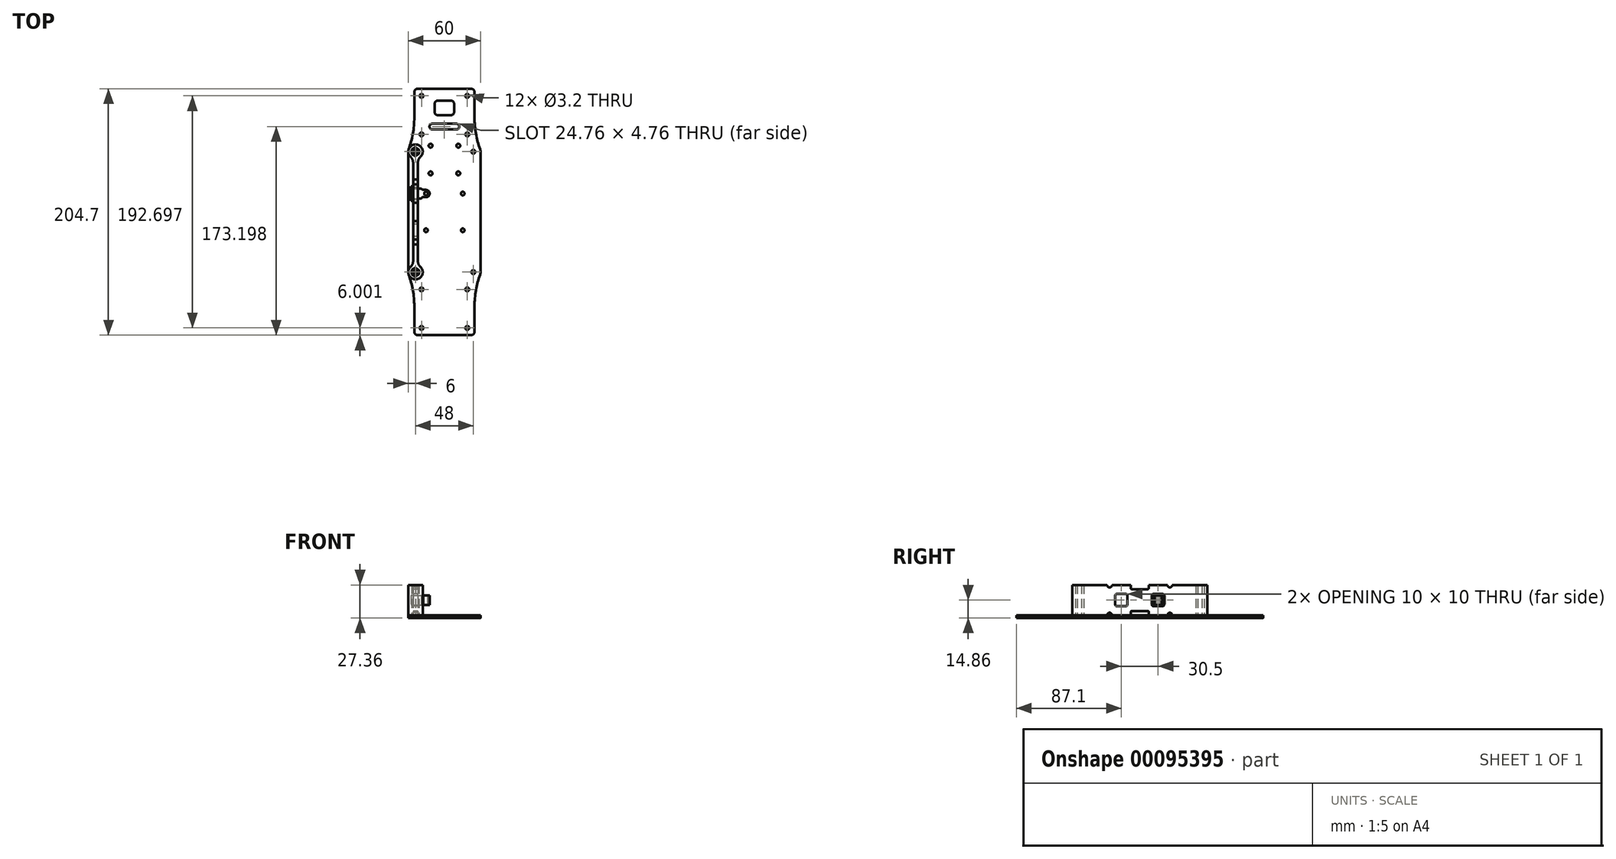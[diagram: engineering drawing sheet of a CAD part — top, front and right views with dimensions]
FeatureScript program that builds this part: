
annotation { "Feature Type Name" : "Feature", "Feature Type Description" : "" }
export const myFeature = defineFeature(function(context is Context, id is Id, definition is map)
    precondition{}
    {
        {
            var Q0;
            Q0=qCreatedBy(makeId("Top.planeOp"),FACE);
            var sketch = newSketch(context, id + "F0", { "sketchPlane" : qUnion([Q0])});
            skLineSegment(sketch, "E0", {"start": v(0, 102.35) * mm, "end": v(-22, 102.35) * mm});
            skLineSegment(sketch, "E1", {"start": v(-25, 99.35) * mm, "end": v(-25, 78.35) * mm});
            skLineSegment(sketch, "E2", {"start": v(-22, -102.35) * mm, "end": v(0, -102.35) * mm});
            skArc(sketch, "E3.filletArc", {"start": v(-22, 102.35) * mm, "mid": v(-24.12, 101.47) * mm, "end": v(-25, 99.35) * mm});
            skArc(sketch, "E4.filletArc", {"start": v(-25, -99.35) * mm, "mid": v(-24.12, -101.47) * mm, "end": v(-22, -102.35) * mm});
            skArc(sketch, "E5.filletArc", {"start": v(-29.64, 52.05) * mm, "mid": v(-29.9, 51.04) * mm, "end": v(-30, 50) * mm});
            skArc(sketch, "E6.MirrorCS", {"start": v(-29.64, -52.05) * mm, "mid": v(-29.9, -51.04) * mm, "end": v(-30, -50) * mm});
            skLineSegment(sketch, "E7.trimOffspring", {"start": v(-25, -78.35) * mm, "end": v(-25, -99.35) * mm});
            skArc(sketch, "E8", {"start": v(-25, -78.35) * mm, "mid": v(-26.17, -65) * mm, "end": v(-29.64, -52.05) * mm});
            skArc(sketch, "E9", {"start": v(-29.64, 52.05) * mm, "mid": v(-26.17, 65) * mm, "end": v(-25, 78.35) * mm});
            skCircle(sketch, "E10", {"center": v(0, 0) * mm, "radius": 125 * mm, "construction": true});
            skLineSegment(sketch, "E11", {"start": v(-95.76, 80.35) * mm, "end": v(95.76, -80.35) * mm, "construction": true});
            skLineSegment(sketch, "E12", {"start": v(95.76, 80.35) * mm, "end": v(-95.76, -80.35) * mm, "construction": true});
            skLineSegment(sketch, "E13", {"start": v(0, 125) * mm, "end": v(0, -125) * mm, "construction": true});
            skLineSegment(sketch, "E14", {"start": v(-95.76, 80.35) * mm, "end": v(95.76, 80.35) * mm, "construction": true});
            skLineSegment(sketch, "E15", {"start": v(-95.76, -80.35) * mm, "end": v(95.76, -80.35) * mm, "construction": true});
            skLineSegment(sketch, "E16", {"start": v(-30, 50) * mm, "end": v(-30, -50) * mm});
            skLineSegment(sketch, "E17.MirrorCS", {"start": v(0, 102.35) * mm, "end": v(22, 102.35) * mm});
            skArc(sketch, "E18.MirrorCS", {"start": v(22, 102.35) * mm, "mid": v(24.12, 101.47) * mm, "end": v(25, 99.35) * mm});
            skLineSegment(sketch, "E19.MirrorCS", {"start": v(25, 99.35) * mm, "end": v(25, 78.35) * mm});
            skArc(sketch, "E20.MirrorCS", {"start": v(29.64, 52.05) * mm, "mid": v(26.17, 65) * mm, "end": v(25, 78.35) * mm});
            skArc(sketch, "E21.MirrorCS", {"start": v(29.64, 52.05) * mm, "mid": v(29.9, 51.04) * mm, "end": v(30, 50) * mm});
            skLineSegment(sketch, "E22.MirrorCS", {"start": v(30, 50) * mm, "end": v(30, -50) * mm});
            skArc(sketch, "E23.MirrorCS", {"start": v(29.64, -52.05) * mm, "mid": v(29.9, -51.04) * mm, "end": v(30, -50) * mm});
            skArc(sketch, "E24.MirrorCS", {"start": v(25, -78.35) * mm, "mid": v(26.17, -65) * mm, "end": v(29.64, -52.05) * mm});
            skArc(sketch, "E25.MirrorCS", {"start": v(25, -99.35) * mm, "mid": v(24.12, -101.47) * mm, "end": v(22, -102.35) * mm});
            skLineSegment(sketch, "E26.MirrorCS", {"start": v(22, -102.35) * mm, "end": v(0, -102.35) * mm});
            skLineSegment(sketch, "E27.MirrorCS", {"start": v(25, -78.35) * mm, "end": v(25, -99.35) * mm});
            skSolve(sketch);
        }
        {
            var Q0;
            Q0 = qSketchRegion(id + "F0", true);
            extrude(context, id + "F1", {"entities" : qUnion([Q0]), "oppositeDirection" : true, "depth" : 2.36 * mm});
        }
        {
            var Q0;
            Q0=makeQuery(id+"F1.opExtrude","CAP_FACE",FACE,{"disambiguationData":[OSD([sQuery(id+"F0.wireOp",EDGE,"E0"),sQuery(id+"F0.wireOp",EDGE,"E1"),sQuery(id+"F0.wireOp",EDGE,"E2"),sQuery(id+"F0.wireOp",EDGE,"E3.filletArc"),sQuery(id+"F0.wireOp",EDGE,"E4.filletArc"),sQuery(id+"F0.wireOp",EDGE,"d22b67ea-32aa-4b1a-bfbd-94ae52c1f5b30.MirrorCS"),sQuery(id+"F0.wireOp",EDGE,"d22b67ea-32aa-4b1a-bfbd-94ae52c1f5b31.MirrorCS"),sQuery(id+"F0.wireOp",EDGE,"d22b67ea-32aa-4b1a-bfbd-94ae52c1f5b32.MirrorCS"),sQuery(id+"F0.wireOp",EDGE,"d22b67ea-32aa-4b1a-bfbd-94ae52c1f5b33.MirrorCS"),sQuery(id+"F0.wireOp",EDGE,"d22b67ea-32aa-4b1a-bfbd-94ae52c1f5b34.MirrorCS")])],"isStart":true});
            var sketch = newSketch(context, id + "F2", { "sketchPlane" : qUnion([Q0])});
            skCircle(sketch, "E28", {"center": v(-19, 96.35) * mm, "radius": 1.6 * mm});
            skCircle(sketch, "E29", {"center": v(-19, 64.35) * mm, "radius": 1.6 * mm});
            skCircle(sketch, "E30", {"center": v(-19, -96.35) * mm, "radius": 1.6 * mm});
            skCircle(sketch, "E31", {"center": v(-19, -64.35) * mm, "radius": 1.6 * mm});
            skCircle(sketch, "E32", {"center": v(-24, -50) * mm, "radius": 1.6 * mm});
            skCircle(sketch, "E33", {"center": v(-24, 50) * mm, "radius": 1.6 * mm});
            skLineSegment(sketch, "E34", {"start": v(-19, 96.35) * mm, "end": v(-19, -96.35) * mm, "construction": true});
            skCircle(sketch, "E35.MirrorC", {"center": v(19, 96.35) * mm, "radius": 1.6 * mm});
            skCircle(sketch, "E36.MirrorC", {"center": v(19, 64.35) * mm, "radius": 1.6 * mm});
            skCircle(sketch, "E37.MirrorC", {"center": v(24, 50) * mm, "radius": 1.6 * mm});
            skCircle(sketch, "E38.MirrorC", {"center": v(24, -50) * mm, "radius": 1.6 * mm});
            skCircle(sketch, "E39.MirrorC", {"center": v(19, -64.35) * mm, "radius": 1.6 * mm});
            skCircle(sketch, "E40.MirrorC", {"center": v(19, -96.35) * mm, "radius": 1.6 * mm});
            skLineSegment(sketch, "E41", {"start": v(-15.25, 15.25) * mm, "end": v(-15.25, -15.25) * mm, "construction": true});
            skPoint(sketch, "E42", {"position": v(-15.25, 0) * mm});
            skLineSegment(sketch, "E43", {"start": v(0, 0) * mm, "end": v(-30, 0) * mm, "construction": true});
            skCircle(sketch, "E44", {"center": v(-15.25, -15.25) * mm, "radius": 1.5 * mm});
            skCircle(sketch, "E45", {"center": v(-15.25, 15.25) * mm, "radius": 1.5 * mm});
            skCircle(sketch, "E46.MirrorC", {"center": v(15.25, 15.25) * mm, "radius": 1.5 * mm});
            skCircle(sketch, "E47.MirrorC", {"center": v(15.25, -15.25) * mm, "radius": 1.5 * mm});
            skSolve(sketch);
        }
        {
            var Q0;
            Q0 = qSketchRegion(id + "F2", true);
            extrude(context, id + "F3", {"entities" : qUnion([Q0]), "operationType" : NewBodyOperationType.REMOVE, "endBound" : BoundingType.THROUGH_ALL, "oppositeDirection" : true, "depth" : 25.4 * mm});
        }
        {
            var Q0;
            Q0=qCreatedBy(makeId("Top.planeOp"),FACE);
            var sketch = newSketch(context, id + "F4", { "sketchPlane" : qUnion([Q0])});
            skCircle(sketch, "E48.cCircle", {"center": v(-24, 50) * mm, "radius": 3.1 * mm, "construction": true});
            skLineSegment(sketch, "E48.0", {"start": v(-24, 53.58) * mm, "end": v(-20.9, 51.79) * mm, "construction": true});
            skLineSegment(sketch, "E48.1", {"start": v(-20.9, 51.79) * mm, "end": v(-20.9, 48.21) * mm, "construction": true});
            skLineSegment(sketch, "E48.2", {"start": v(-20.9, 48.21) * mm, "end": v(-24, 46.42) * mm, "construction": true});
            skLineSegment(sketch, "E48.3", {"start": v(-24, 46.42) * mm, "end": v(-27.1, 48.21) * mm, "construction": true});
            skLineSegment(sketch, "E48.4", {"start": v(-27.1, 48.21) * mm, "end": v(-27.1, 51.79) * mm, "construction": true});
            skLineSegment(sketch, "E48.5", {"start": v(-27.1, 51.79) * mm, "end": v(-24, 53.58) * mm, "construction": true});
            skPoint(sketch, "E48.0.midPoint", {"position": v(-22.45, 52.68) * mm});
            skArc(sketch, "E49", {"start": v(-20, 45.53) * mm, "mid": v(-24, 56) * mm, "end": v(-28, 45.53) * mm});
            skArc(sketch, "E50", {"start": v(-28, -45.53) * mm, "mid": v(-24, -56) * mm, "end": v(-20, -45.53) * mm});
            skLineSegment(sketch, "E51", {"start": v(-26, 41.06) * mm, "end": v(-26, -41.06) * mm});
            skLineSegment(sketch, "E52", {"start": v(-22, 41.06) * mm, "end": v(-22, -41.06) * mm});
            skPoint(sketch, "E53.visualSharp", {"position": v(-26, 44.34) * mm});
            skArc(sketch, "E53.filletArc", {"start": v(-26, 41.06) * mm, "mid": v(-26.52, 43.5) * mm, "end": v(-28, 45.53) * mm});
            skPoint(sketch, "E54.visualSharp", {"position": v(-22, 44.34) * mm});
            skArc(sketch, "E54.filletArc", {"start": v(-20, 45.53) * mm, "mid": v(-21.48, 43.5) * mm, "end": v(-22, 41.06) * mm});
            skPoint(sketch, "E55.visualSharp", {"position": v(-22, -44.34) * mm});
            skArc(sketch, "E55.filletArc", {"start": v(-22, -41.06) * mm, "mid": v(-21.48, -43.5) * mm, "end": v(-20, -45.53) * mm});
            skPoint(sketch, "E56.visualSharp", {"position": v(-26, -44.34) * mm});
            skArc(sketch, "E56.filletArc", {"start": v(-28, -45.53) * mm, "mid": v(-26.52, -43.5) * mm, "end": v(-26, -41.06) * mm});
            skLineSegment(sketch, "E57", {"start": v(-24, 50) * mm, "end": v(-24, -50) * mm, "construction": true});
            skSolve(sketch);
        }
        {
            var Q0;
            Q0 = qSketchRegion(id + "F4", true);
            extrude(context, id + "F5", {"entities" : qUnion([Q0]), "depth" : 25 * mm});
        }
        {
            var Q0;
            Q0=makeQuery(id+"F5.opExtrude","CAP_FACE",FACE,{"disambiguationData":[OSD([sQuery(id+"F4.wireOp",EDGE,"E49"),sQuery(id+"F4.wireOp",EDGE,"E50"),sQuery(id+"F4.wireOp",EDGE,"E51"),sQuery(id+"F4.wireOp",EDGE,"E52"),sQuery(id+"F4.wireOp",EDGE,"E53.filletArc"),sQuery(id+"F4.wireOp",EDGE,"E54.filletArc"),sQuery(id+"F4.wireOp",EDGE,"E55.filletArc"),sQuery(id+"F4.wireOp",EDGE,"E56.filletArc")])],"isStart":true});
            var sketch = newSketch(context, id + "F6", { "sketchPlane" : qUnion([Q0])});
            skCircle(sketch, "E58.cCircle", {"center": v(-24, -50) * mm, "radius": 3.05 * mm, "construction": true});
            skLineSegment(sketch, "E58.0", {"start": v(-27.05, -48.24) * mm, "end": v(-24, -46.48) * mm});
            skLineSegment(sketch, "E58.1", {"start": v(-24, -46.48) * mm, "end": v(-20.95, -48.24) * mm});
            skLineSegment(sketch, "E58.2", {"start": v(-20.95, -48.24) * mm, "end": v(-20.95, -51.76) * mm});
            skLineSegment(sketch, "E58.3", {"start": v(-20.95, -51.76) * mm, "end": v(-24, -53.52) * mm});
            skLineSegment(sketch, "E58.4", {"start": v(-24, -53.52) * mm, "end": v(-27.05, -51.76) * mm});
            skLineSegment(sketch, "E58.5", {"start": v(-27.05, -51.76) * mm, "end": v(-27.05, -48.24) * mm});
            skPoint(sketch, "E58.0.midPoint", {"position": v(-25.53, -47.36) * mm});
            skCircle(sketch, "E59.cCircle", {"center": v(-24, 50) * mm, "radius": 3.05 * mm, "construction": true});
            skLineSegment(sketch, "E59.0", {"start": v(-27.05, 51.76) * mm, "end": v(-24, 53.52) * mm});
            skLineSegment(sketch, "E59.1", {"start": v(-24, 53.52) * mm, "end": v(-20.95, 51.76) * mm});
            skLineSegment(sketch, "E59.2", {"start": v(-20.95, 51.76) * mm, "end": v(-20.95, 48.24) * mm});
            skLineSegment(sketch, "E59.3", {"start": v(-20.95, 48.24) * mm, "end": v(-24, 46.48) * mm});
            skLineSegment(sketch, "E59.4", {"start": v(-24, 46.48) * mm, "end": v(-27.05, 48.24) * mm});
            skLineSegment(sketch, "E59.5", {"start": v(-27.05, 48.24) * mm, "end": v(-27.05, 51.76) * mm});
            skPoint(sketch, "E59.0.midPoint", {"position": v(-25.52, 52.64) * mm});
            skSolve(sketch);
        }
        {
            var Q0;
            Q0 = qSketchRegion(id + "F6", true);
            var Q1;
            Q1=makeQuery(id+"F5.opExtrude","CAP_FACE",FACE,{"disambiguationData":[OSD([sQuery(id+"F4.wireOp",EDGE,"E49"),sQuery(id+"F4.wireOp",EDGE,"E50"),sQuery(id+"F4.wireOp",EDGE,"E51"),sQuery(id+"F4.wireOp",EDGE,"E52"),sQuery(id+"F4.wireOp",EDGE,"E53.filletArc"),sQuery(id+"F4.wireOp",EDGE,"E54.filletArc"),sQuery(id+"F4.wireOp",EDGE,"E55.filletArc"),sQuery(id+"F4.wireOp",EDGE,"E56.filletArc")])],"isStart":false});
            extrude(context, id + "F7", {"entities" : qUnion([Q0]), "operationType" : NewBodyOperationType.REMOVE, "endBound" : BoundingType.UP_TO_SURFACE, "oppositeDirection" : true, "endBoundEntityFace" : qUnion([Q1]), "depth" : 25 * mm});
        }
        {
            var Q0;
            Q0=makeQuery(id+"F5.opExtrude","SWEPT_FACE",FACE,{"disambiguationData":[OSD([sQuery(id+"F4.wireOp",EDGE,"E51")])]});
            var sketch = newSketch(context, id + "F8", { "sketchPlane" : qUnion([Q0])});
            skLineSegment(sketch, "E60", {"start": v(-21.13, 12.5) * mm, "end": v(21.13, 12.5) * mm, "construction": true});
            skLineSegment(sketch, "E61.bottom", {"start": v(-11.25, 17.5) * mm, "end": v(-19.25, 17.5) * mm});
            skLineSegment(sketch, "E61.top", {"start": v(-11.25, 7.5) * mm, "end": v(-19.25, 7.5) * mm});
            skLineSegment(sketch, "E61.left", {"start": v(-10.25, 16.5) * mm, "end": v(-10.25, 8.5) * mm});
            skLineSegment(sketch, "E61.right", {"start": v(-20.25, 16.5) * mm, "end": v(-20.25, 8.5) * mm});
            skPoint(sketch, "E61.middle", {"position": v(-15.25, 12.5) * mm});
            skPoint(sketch, "E62.visualSharp", {"position": v(-20.25, 17.5) * mm});
            skArc(sketch, "E62.filletArc", {"start": v(-19.25, 17.5) * mm, "mid": v(-19.96, 17.2) * mm, "end": v(-20.25, 16.5) * mm});
            skPoint(sketch, "E63.visualSharp", {"position": v(-20.25, 7.5) * mm});
            skArc(sketch, "E63.filletArc", {"start": v(-20.25, 8.5) * mm, "mid": v(-19.96, 7.8) * mm, "end": v(-19.25, 7.5) * mm});
            skPoint(sketch, "E64.visualSharp", {"position": v(-10.25, 7.5) * mm});
            skArc(sketch, "E64.filletArc", {"start": v(-11.25, 7.5) * mm, "mid": v(-10.54, 7.8) * mm, "end": v(-10.25, 8.5) * mm});
            skPoint(sketch, "E65.visualSharp", {"position": v(-10.25, 17.5) * mm});
            skArc(sketch, "E65.filletArc", {"start": v(-10.25, 16.5) * mm, "mid": v(-10.54, 17.2) * mm, "end": v(-11.25, 17.5) * mm});
            skLineSegment(sketch, "E66.bottom", {"start": v(-7.5, 0) * mm, "end": v(7.5, 0) * mm});
            skLineSegment(sketch, "E66.top", {"start": v(-6.5, 3.5) * mm, "end": v(6.5, 3.5) * mm});
            skLineSegment(sketch, "E66.left", {"start": v(-7.5, 0) * mm, "end": v(-7.5, 2.5) * mm});
            skLineSegment(sketch, "E66.right", {"start": v(7.5, 0) * mm, "end": v(7.5, 2.5) * mm});
            skPoint(sketch, "E67.visualSharp", {"position": v(-7.5, 3.5) * mm});
            skArc(sketch, "E67.filletArc", {"start": v(-6.5, 3.5) * mm, "mid": v(-7.2, 3.2) * mm, "end": v(-7.5, 2.5) * mm});
            skPoint(sketch, "E68.visualSharp", {"position": v(7.5, 3.5) * mm});
            skArc(sketch, "E68.filletArc", {"start": v(7.5, 2.5) * mm, "mid": v(7.2, 3.2) * mm, "end": v(6.5, 3.5) * mm});
            skArc(sketch, "E69", {"start": v(-27, 25) * mm, "mid": v(-25, 23) * mm, "end": v(-23, 25) * mm});
            skLineSegment(sketch, "E70", {"start": v(-25, 25) * mm, "end": v(-25, 0) * mm, "construction": true});
            skArc(sketch, "E71", {"start": v(-23, 0) * mm, "mid": v(-25, 2) * mm, "end": v(-27, 0) * mm});
            skLineSegment(sketch, "E72", {"start": v(-27, 25) * mm, "end": v(-23, 25) * mm});
            skLineSegment(sketch, "E73", {"start": v(-27, 0) * mm, "end": v(-23, 0) * mm});
            skLineSegment(sketch, "E74", {"start": v(0, 25) * mm, "end": v(0, 0) * mm, "construction": true});
            skPoint(sketch, "E75", {"position": v(0, 12.5) * mm});
            skArc(sketch, "E76.MirrorCS", {"start": v(11.25, 7.5) * mm, "mid": v(10.54, 7.8) * mm, "end": v(10.25, 8.5) * mm});
            skArc(sketch, "E77.MirrorCS", {"start": v(10.25, 16.5) * mm, "mid": v(10.54, 17.2) * mm, "end": v(11.25, 17.5) * mm});
            skArc(sketch, "E78.MirrorCS", {"start": v(20.25, 8.5) * mm, "mid": v(19.96, 7.8) * mm, "end": v(19.25, 7.5) * mm});
            skArc(sketch, "E79.MirrorCS", {"start": v(19.25, 17.5) * mm, "mid": v(19.96, 17.2) * mm, "end": v(20.25, 16.5) * mm});
            skPoint(sketch, "E80.MirrorP", {"position": v(10.25, 17.5) * mm});
            skLineSegment(sketch, "E81.MirrorCS", {"start": v(20.25, 16.5) * mm, "end": v(20.25, 8.5) * mm});
            skLineSegment(sketch, "E82.MirrorCS", {"start": v(10.25, 16.5) * mm, "end": v(10.25, 8.5) * mm});
            skLineSegment(sketch, "E83.MirrorCS", {"start": v(11.25, 17.5) * mm, "end": v(19.25, 17.5) * mm});
            skLineSegment(sketch, "E84.MirrorCS", {"start": v(11.25, 7.5) * mm, "end": v(19.25, 7.5) * mm});
            skPoint(sketch, "E85.MirrorP", {"position": v(20.25, 7.5) * mm});
            skPoint(sketch, "E86.MirrorP", {"position": v(15.25, 12.5) * mm});
            skPoint(sketch, "E87.MirrorP", {"position": v(20.25, 17.5) * mm});
            skPoint(sketch, "E88.MirrorP", {"position": v(10.25, 7.5) * mm});
            skLineSegment(sketch, "E89.MirrorCS", {"start": v(27, 25) * mm, "end": v(23, 25) * mm});
            skLineSegment(sketch, "E90.MirrorCS", {"start": v(25, 25) * mm, "end": v(25, 0) * mm, "construction": true});
            skArc(sketch, "E91.MirrorCS", {"start": v(27, 25) * mm, "mid": v(25, 23) * mm, "end": v(23, 25) * mm});
            skLineSegment(sketch, "E92.MirrorCS", {"start": v(27, 0) * mm, "end": v(23, 0) * mm});
            skArc(sketch, "E93.MirrorCS", {"start": v(23, 0) * mm, "mid": v(25, 2) * mm, "end": v(27, 0) * mm});
            skArc(sketch, "E94.MirrorCS", {"start": v(-6.5, 21.5) * mm, "mid": v(-7.2, 21.8) * mm, "end": v(-7.5, 22.5) * mm});
            skArc(sketch, "E95.MirrorCS", {"start": v(7.5, 22.5) * mm, "mid": v(7.2, 21.8) * mm, "end": v(6.5, 21.5) * mm});
            skPoint(sketch, "E96.MirrorP", {"position": v(-7.5, 21.5) * mm});
            skLineSegment(sketch, "E97.MirrorCS", {"start": v(-6.5, 21.5) * mm, "end": v(6.5, 21.5) * mm});
            skLineSegment(sketch, "E98.MirrorCS", {"start": v(-7.5, 25) * mm, "end": v(-7.5, 22.5) * mm});
            skPoint(sketch, "E99.MirrorP", {"position": v(7.5, 21.5) * mm});
            skLineSegment(sketch, "E100.MirrorCS", {"start": v(7.5, 25) * mm, "end": v(7.5, 22.5) * mm});
            skLineSegment(sketch, "E101.MirrorCS", {"start": v(-7.5, 25) * mm, "end": v(7.5, 25) * mm});
            skSolve(sketch);
        }
        {
            var Q0;
            Q0 = qSketchRegion(id + "F8", true);
            var Q1;
            Q1=makeQuery(id+"F5.opExtrude","SWEPT_FACE",FACE,{"disambiguationData":[OSD([sQuery(id+"F4.wireOp",EDGE,"E52")])]});
            extrude(context, id + "F9", {"entities" : qUnion([Q0]), "operationType" : NewBodyOperationType.REMOVE, "endBound" : BoundingType.UP_TO_SURFACE, "oppositeDirection" : true, "endBoundEntityFace" : qUnion([Q1]), "depth" : 25 * mm});
        }
        {
            var Q0;
            Q0=qCreatedBy(makeId("Top.planeOp"),FACE);
            cPlane(context, id + "F10", {"entities" : qUnion([Q0]), "cplaneType" : CPlaneType.OFFSET, "offset" : 12.5 * mm, "width" : 150 * mm, "height" : 150 * mm});
        }
        {
            var Q0;
            Q0=qCreatedBy(id+"F10.planeOp",FACE);
            var sketch = newSketch(context, id + "F11", { "sketchPlane" : qUnion([Q0])});
            skLineSegment(sketch, "E102", {"start": v(-26.25, 21.25) * mm, "end": v(-26.25, 19.75) * mm});
            skLineSegment(sketch, "E103", {"start": v(-25.75, 19.25) * mm, "end": v(-19.25, 19.25) * mm});
            skLineSegment(sketch, "E104", {"start": v(-19.25, 19.25) * mm, "end": v(-18.25, 18.25) * mm});
            skLineSegment(sketch, "E105", {"start": v(-18.25, 18.25) * mm, "end": v(-15.25, 18.25) * mm});
            skLineSegment(sketch, "E106", {"start": v(-6.48, 15.25) * mm, "end": v(-35.06, 15.25) * mm, "construction": true});
            skArc(sketch, "E107", {"start": v(-12.25, 15.25) * mm, "mid": v(-13.13, 17.37) * mm, "end": v(-15.25, 18.25) * mm});
            skLineSegment(sketch, "E108", {"start": v(-26.25, 21.25) * mm, "end": v(-27.75, 21.25) * mm});
            skLineSegment(sketch, "E109", {"start": v(-27.75, 21.25) * mm, "end": v(-27.75, 15.25) * mm});
            skPoint(sketch, "E110.visualSharp", {"position": v(-26.25, 19.25) * mm});
            skArc(sketch, "E110.filletArc", {"start": v(-26.25, 19.75) * mm, "mid": v(-26.1, 19.4) * mm, "end": v(-25.75, 19.25) * mm});
            skLineSegment(sketch, "E111.MirrorCS", {"start": v(-27.75, 9.25) * mm, "end": v(-27.75, 15.25) * mm});
            skLineSegment(sketch, "E112.MirrorCS", {"start": v(-26.25, 9.25) * mm, "end": v(-27.75, 9.25) * mm});
            skLineSegment(sketch, "E113.MirrorCS", {"start": v(-26.25, 9.25) * mm, "end": v(-26.25, 10.75) * mm});
            skArc(sketch, "E114.MirrorCS", {"start": v(-26.25, 10.75) * mm, "mid": v(-26.1, 11.1) * mm, "end": v(-25.75, 11.25) * mm});
            skLineSegment(sketch, "E115.MirrorCS", {"start": v(-25.75, 11.25) * mm, "end": v(-19.25, 11.25) * mm});
            skLineSegment(sketch, "E116.MirrorCS", {"start": v(-19.25, 11.25) * mm, "end": v(-18.25, 12.25) * mm});
            skLineSegment(sketch, "E117.MirrorCS", {"start": v(-18.25, 12.25) * mm, "end": v(-15.25, 12.25) * mm});
            skArc(sketch, "E118.MirrorCS", {"start": v(-12.25, 15.25) * mm, "mid": v(-13.13, 13.13) * mm, "end": v(-15.25, 12.25) * mm});
            skSolve(sketch);
        }
        {
            var Q0;
            Q0 = qSketchRegion(id + "F11", true);
            extrude(context, id + "F12", {"entities" : qUnion([Q0]), "endBound" : BoundingType.SYMMETRIC, "depth" : 8 * mm});
        }
        {
            var Q0;
            Q0=makeQuery(id+"F12.opExtrude","CAP_FACE",FACE,{"disambiguationData":[OSD([sQuery(id+"F11.wireOp",EDGE,"E102"),sQuery(id+"F11.wireOp",EDGE,"E103"),sQuery(id+"F11.wireOp",EDGE,"E104"),sQuery(id+"F11.wireOp",EDGE,"E105"),sQuery(id+"F11.wireOp",EDGE,"E107"),sQuery(id+"F11.wireOp",EDGE,"E108"),sQuery(id+"F11.wireOp",EDGE,"E109"),sQuery(id+"F11.wireOp",EDGE,"E110.filletArc"),sQuery(id+"F11.wireOp",EDGE,"E111.MirrorCS"),sQuery(id+"F11.wireOp",EDGE,"E112.MirrorCS"),sQuery(id+"F11.wireOp",EDGE,"E113.MirrorCS"),sQuery(id+"F11.wireOp",EDGE,"E114.MirrorCS"),sQuery(id+"F11.wireOp",EDGE,"E115.MirrorCS"),sQuery(id+"F11.wireOp",EDGE,"E116.MirrorCS"),sQuery(id+"F11.wireOp",EDGE,"E117.MirrorCS"),sQuery(id+"F11.wireOp",EDGE,"E118.MirrorCS")])],"isStart":false});
            var sketch = newSketch(context, id + "F13", { "sketchPlane" : qUnion([Q0])});
            skCircle(sketch, "E119", {"center": v(-15.25, 15.25) * mm, "radius": 1.5 * mm});
            skSolve(sketch);
        }
        {
            var Q0;
            Q0 = qSketchRegion(id + "F13", true);
            var Q1;
            Q1=makeQuery(id+"F12.opExtrude","CAP_FACE",FACE,{"disambiguationData":[OSD([sQuery(id+"F11.wireOp",EDGE,"E102"),sQuery(id+"F11.wireOp",EDGE,"E103"),sQuery(id+"F11.wireOp",EDGE,"E104"),sQuery(id+"F11.wireOp",EDGE,"E105"),sQuery(id+"F11.wireOp",EDGE,"E107"),sQuery(id+"F11.wireOp",EDGE,"E108"),sQuery(id+"F11.wireOp",EDGE,"E109"),sQuery(id+"F11.wireOp",EDGE,"E110.filletArc"),sQuery(id+"F11.wireOp",EDGE,"E111.MirrorCS"),sQuery(id+"F11.wireOp",EDGE,"E112.MirrorCS"),sQuery(id+"F11.wireOp",EDGE,"E113.MirrorCS"),sQuery(id+"F11.wireOp",EDGE,"E114.MirrorCS"),sQuery(id+"F11.wireOp",EDGE,"E115.MirrorCS"),sQuery(id+"F11.wireOp",EDGE,"E116.MirrorCS"),sQuery(id+"F11.wireOp",EDGE,"E117.MirrorCS"),sQuery(id+"F11.wireOp",EDGE,"E118.MirrorCS")])],"isStart":true});
            extrude(context, id + "F14", {"entities" : qUnion([Q0]), "operationType" : NewBodyOperationType.REMOVE, "endBound" : BoundingType.UP_TO_SURFACE, "oppositeDirection" : true, "endBoundEntityFace" : qUnion([Q1]), "depth" : 25 * mm});
        }
        {
            var Q0;
            Q0=qCreatedBy(makeId("Top.planeOp"),FACE);
            var sketch = newSketch(context, id + "F15", { "sketchPlane" : qUnion([Q0])});
            skLineSegment(sketch, "E120.bottom", {"start": v(-10, 73.23) * mm, "end": v(10, 73.23) * mm});
            skLineSegment(sketch, "E120.top", {"start": v(-10, 68.47) * mm, "end": v(10, 68.47) * mm});
            skPoint(sketch, "E121", {"position": v(0, 73.23) * mm});
            skArc(sketch, "E122", {"start": v(-10, 73.23) * mm, "mid": v(-12.38, 70.85) * mm, "end": v(-10, 68.47) * mm});
            skArc(sketch, "E123", {"start": v(10, 68.47) * mm, "mid": v(12.38, 70.85) * mm, "end": v(10, 73.23) * mm});
            skLineSegment(sketch, "E124.bottom", {"start": v(-5.62, 92.35) * mm, "end": v(5.62, 92.35) * mm});
            skLineSegment(sketch, "E124.top", {"start": v(-5.62, 80.35) * mm, "end": v(5.62, 80.35) * mm});
            skLineSegment(sketch, "E124.left", {"start": v(-8, 89.97) * mm, "end": v(-8, 82.73) * mm});
            skLineSegment(sketch, "E124.right", {"start": v(8, 89.97) * mm, "end": v(8, 82.73) * mm});
            skPoint(sketch, "E125", {"position": v(0, 92.35) * mm});
            skPoint(sketch, "E126.visualSharp", {"position": v(-8, 92.35) * mm});
            skArc(sketch, "E126.filletArc", {"start": v(-5.62, 92.35) * mm, "mid": v(-7.3, 91.65) * mm, "end": v(-8, 89.97) * mm});
            skPoint(sketch, "E127.visualSharp", {"position": v(-8, 80.35) * mm});
            skArc(sketch, "E127.filletArc", {"start": v(-8, 82.73) * mm, "mid": v(-7.3, 81.05) * mm, "end": v(-5.62, 80.35) * mm});
            skPoint(sketch, "E128.visualSharp", {"position": v(8, 80.35) * mm});
            skArc(sketch, "E128.filletArc", {"start": v(5.62, 80.35) * mm, "mid": v(7.3, 81.05) * mm, "end": v(8, 82.73) * mm});
            skPoint(sketch, "E129.visualSharp", {"position": v(8, 92.35) * mm});
            skArc(sketch, "E129.filletArc", {"start": v(8, 89.97) * mm, "mid": v(7.3, 91.65) * mm, "end": v(5.62, 92.35) * mm});
            skLineSegment(sketch, "E130.bottom", {"start": v(-11.5, 55) * mm, "end": v(11.5, 55) * mm, "construction": true});
            skLineSegment(sketch, "E130.top", {"start": v(-11.5, 32) * mm, "end": v(11.5, 32) * mm, "construction": true});
            skLineSegment(sketch, "E130.left", {"start": v(-11.5, 55) * mm, "end": v(-11.5, 32) * mm, "construction": true});
            skLineSegment(sketch, "E130.right", {"start": v(11.5, 55) * mm, "end": v(11.5, 32) * mm, "construction": true});
            skPoint(sketch, "E131", {"position": v(0, 55) * mm});
            skCircle(sketch, "E132", {"center": v(-11.5, 55) * mm, "radius": 1.59 * mm});
            skCircle(sketch, "E133", {"center": v(11.5, 55) * mm, "radius": 1.59 * mm});
            skCircle(sketch, "E134", {"center": v(-11.5, 32) * mm, "radius": 1.59 * mm});
            skCircle(sketch, "E135", {"center": v(11.5, 32) * mm, "radius": 1.59 * mm});
            skSolve(sketch);
        }
        {
            var Q0;
            Q0 = qSketchRegion(id + "F15", true);
            var Q1;
            Q1=makeQuery(id+"F1.opExtrude","CAP_FACE",FACE,{"disambiguationData":[OSD([sQuery(id+"F0.wireOp",EDGE,"E0"),sQuery(id+"F0.wireOp",EDGE,"E1"),sQuery(id+"F0.wireOp",EDGE,"E2"),sQuery(id+"F0.wireOp",EDGE,"E3.filletArc"),sQuery(id+"F0.wireOp",EDGE,"E4.filletArc"),sQuery(id+"F0.wireOp",EDGE,"E5.filletArc"),sQuery(id+"F0.wireOp",EDGE,"E6.MirrorCS"),sQuery(id+"F0.wireOp",EDGE,"E7.trimOffspring"),sQuery(id+"F0.wireOp",EDGE,"E8"),sQuery(id+"F0.wireOp",EDGE,"E9"),sQuery(id+"F0.wireOp",EDGE,"E16"),sQuery(id+"F0.wireOp",EDGE,"E17.MirrorCS"),sQuery(id+"F0.wireOp",EDGE,"E18.MirrorCS"),sQuery(id+"F0.wireOp",EDGE,"E19.MirrorCS"),sQuery(id+"F0.wireOp",EDGE,"E20.MirrorCS"),sQuery(id+"F0.wireOp",EDGE,"E21.MirrorCS"),sQuery(id+"F0.wireOp",EDGE,"E22.MirrorCS"),sQuery(id+"F0.wireOp",EDGE,"E23.MirrorCS"),sQuery(id+"F0.wireOp",EDGE,"E24.MirrorCS"),sQuery(id+"F0.wireOp",EDGE,"E25.MirrorCS"),sQuery(id+"F0.wireOp",EDGE,"E26.MirrorCS"),sQuery(id+"F0.wireOp",EDGE,"E27.MirrorCS")])],"isStart":false});
            extrude(context, id + "F16", {"entities" : qUnion([Q0]), "operationType" : NewBodyOperationType.REMOVE, "endBound" : BoundingType.UP_TO_SURFACE, "oppositeDirection" : true, "endBoundEntityFace" : qUnion([Q1]), "depth" : 25 * mm});
        }
    });
